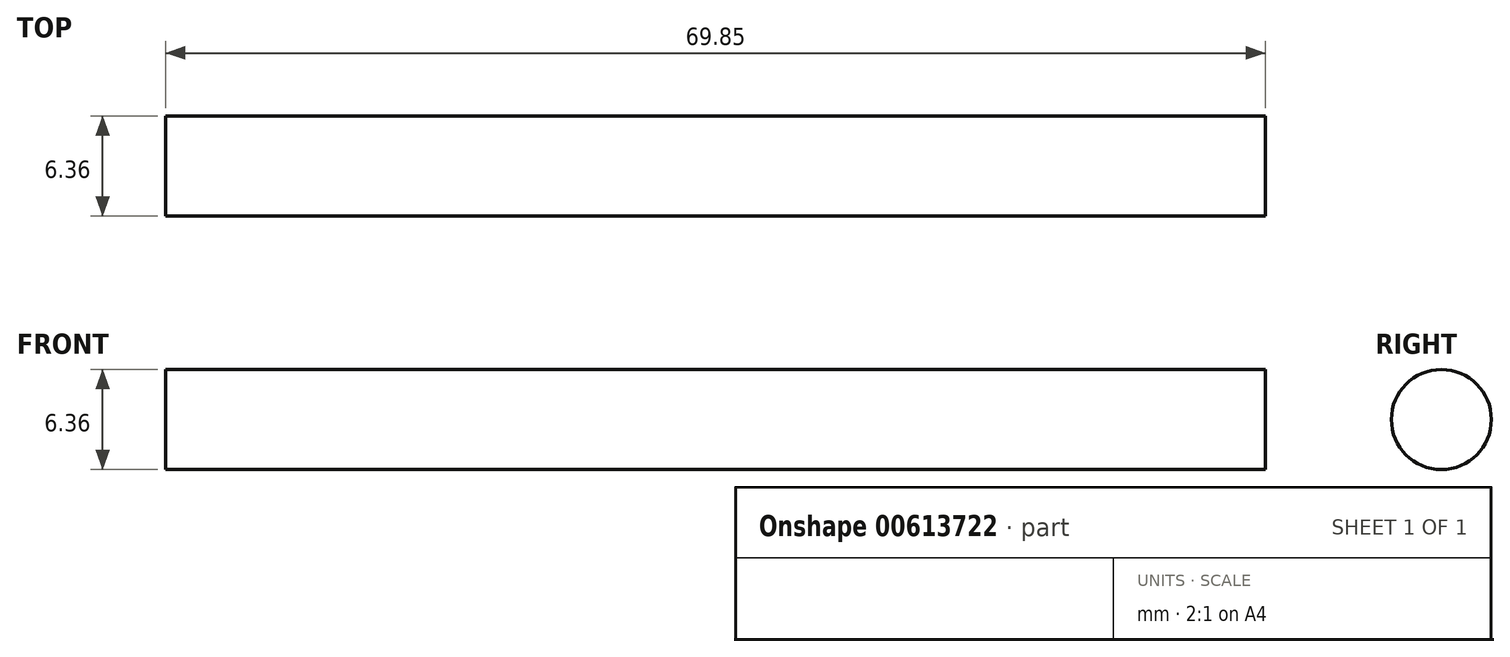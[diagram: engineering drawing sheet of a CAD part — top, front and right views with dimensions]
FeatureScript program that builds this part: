
annotation { "Feature Type Name" : "Feature", "Feature Type Description" : "" }
export const myFeature = defineFeature(function(context is Context, id is Id, definition is map)
    precondition{}
    {
        {
            var Q0;
            Q0=qCreatedBy(makeId("Right.planeOp"),FACE);
            var sketch = newSketch(context, id + "F0", { "sketchPlane" : qUnion([Q0])});
            skCircle(sketch, "E0", {"center": v(0, 0) * mm, "radius": 3.18 * mm});
            skSolve(sketch);
        }
        {
            var Q0;
            Q0=makeQuery(id+"F0.imprint","IMPRINT",FACE,{"disambiguationData":[TD([[makeQuery(id+"F0.imprint","IMPRINT",EDGE,{"derivedFrom":sQuery(id+"F0.wireOp",EDGE,"E0")}),1.0]])]});
            extrude(context, id + "F1", {"entities" : qUnion([Q0]), "depth" : 69.85 * mm, "offsetDistance" : 25.4 * mm});
        }
    });
